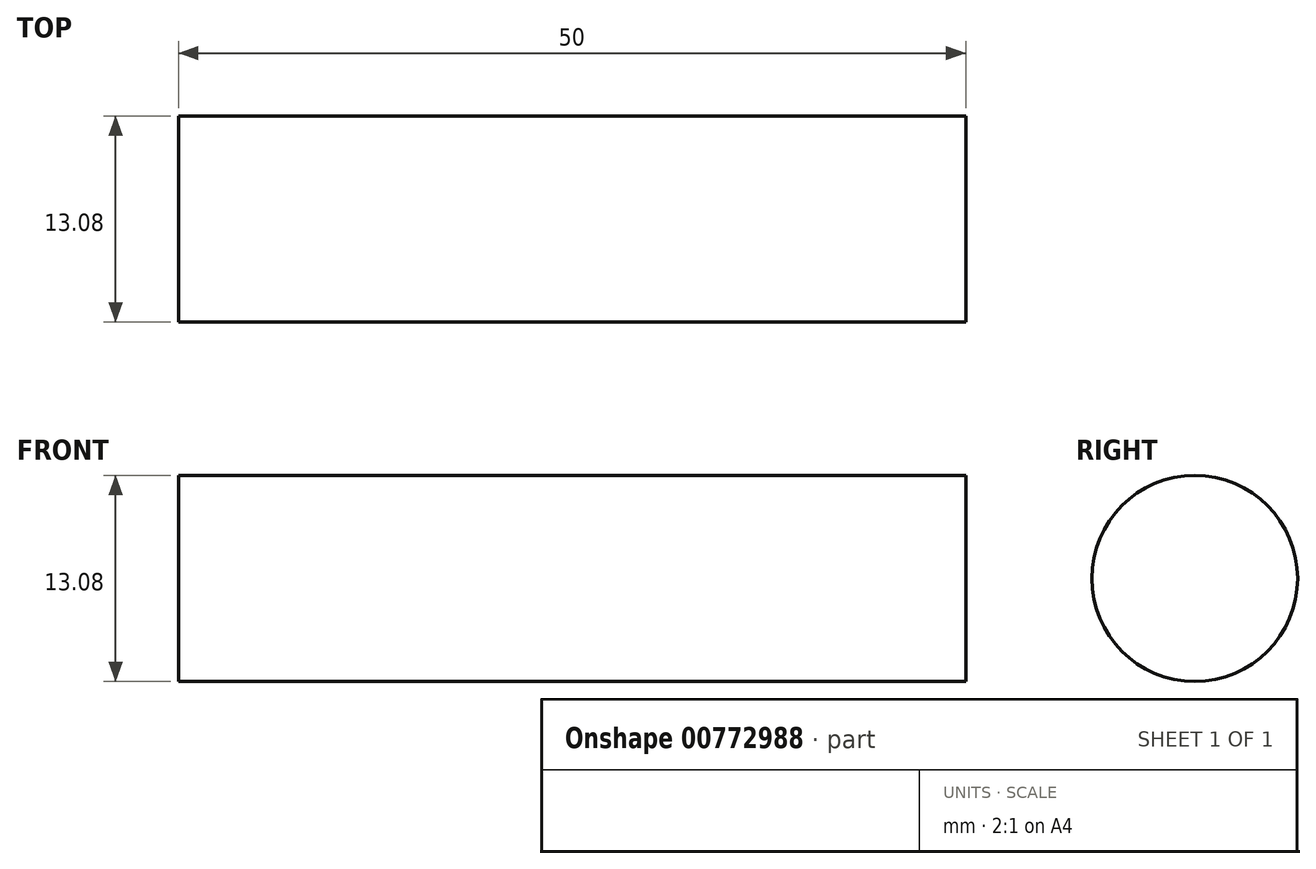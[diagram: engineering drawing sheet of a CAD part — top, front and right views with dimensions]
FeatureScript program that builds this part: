
annotation { "Feature Type Name" : "Feature", "Feature Type Description" : "" }
export const myFeature = defineFeature(function(context is Context, id is Id, definition is map)
    precondition{}
    {
        {
            var Q0;
            Q0=qCreatedBy(makeId("Right.planeOp"),FACE);
            var sketch = newSketch(context, id + "F0", { "sketchPlane" : qUnion([Q0])});
            skCircle(sketch, "E0", {"center": v(0, 0) * mm, "radius": 6.54 * mm});
            skSolve(sketch);
        }
        {
            var Q0;
            Q0=sQuery(id+"F0.wireOp",EDGE,"E0");
            extrude(context, id + "F1", {"bodyType" : ToolBodyType.SURFACE, "surfaceEntities" : qUnion([Q0]), "endBound" : BoundingType.SYMMETRIC, "depth" : 50 * mm, "offsetDistance" : 25 * mm});
        }
    });
